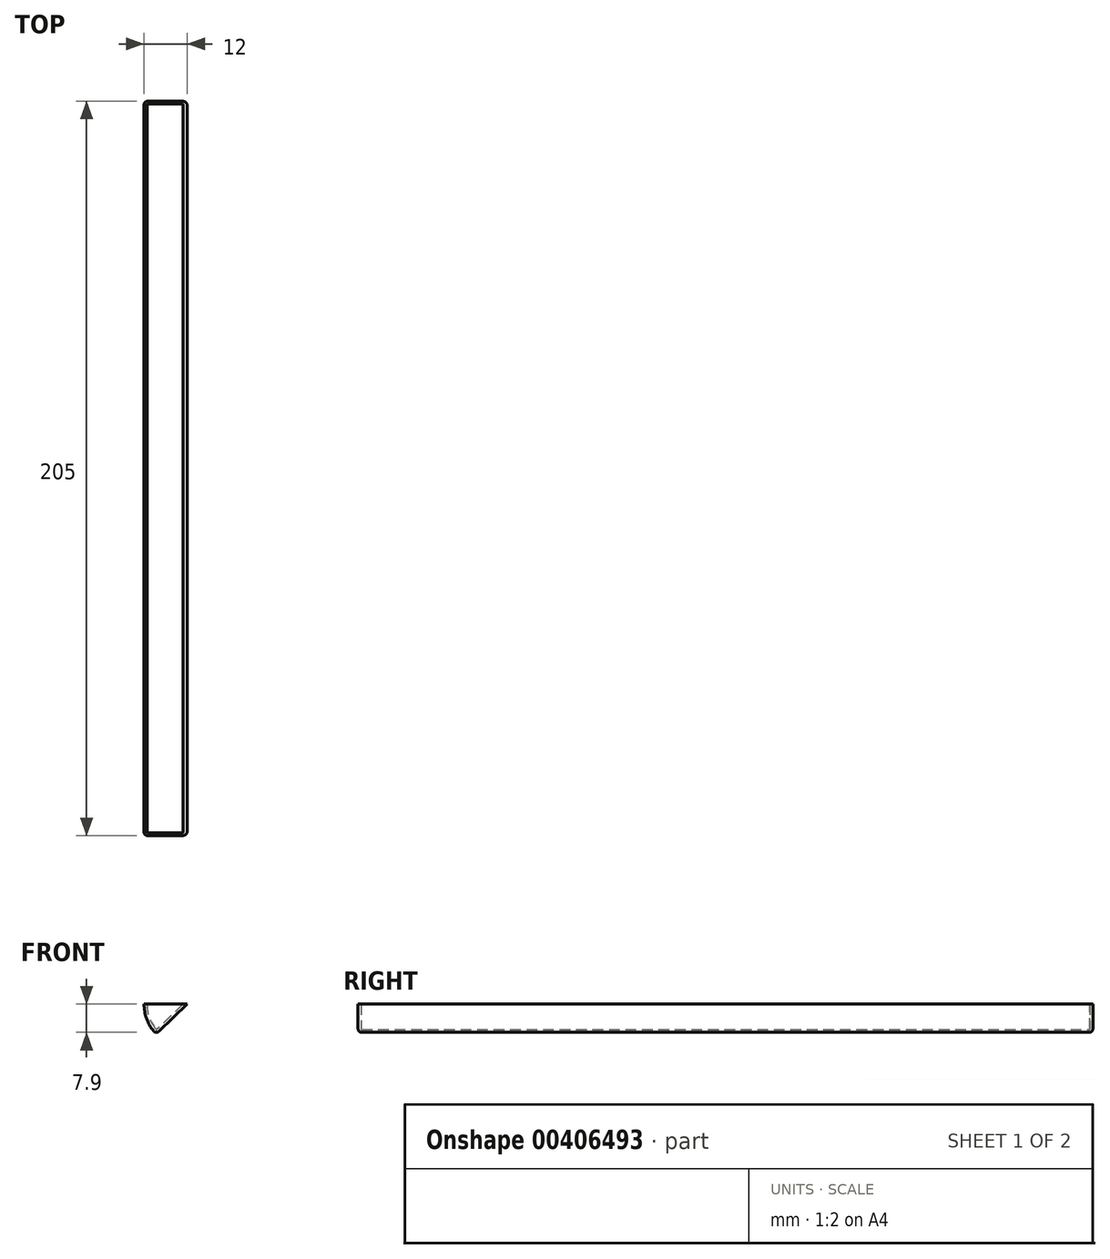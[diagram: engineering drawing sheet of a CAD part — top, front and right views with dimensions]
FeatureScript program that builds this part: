
annotation { "Feature Type Name" : "Feature", "Feature Type Description" : "" }
export const myFeature = defineFeature(function(context is Context, id is Id, definition is map)
    precondition{}
    {
        {
            var Q0;
            Q0=qCreatedBy(makeId("Front.planeOp"),FACE);
            var sketch = newSketch(context, id + "F0", { "sketchPlane" : qUnion([Q0])});
            skPoint(sketch, "E0.middle", {"position": v(0, 0) * mm});
            skLineSegment(sketch, "E1", {"start": v(-12, 0) * mm, "end": v(0, 0) * mm});
            skLineSegment(sketch, "E2", {"start": v(0, 0) * mm, "end": v(-8.62, -8.35) * mm});
            skPoint(sketch, "E0.bottom.start.orphan", {"position": v(-12, 11.63) * mm});
            skPoint(sketch, "E0.right.start.orphan", {"position": v(12, 11.63) * mm});
            skPoint(sketch, "E0.top.end.orphan", {"position": v(12, -11.63) * mm});
            skArc(sketch, "E3", {"start": v(-12, 0) * mm, "mid": v(-11.12, -4.5) * mm, "end": v(-8.62, -8.35) * mm});
            skPoint(sketch, "E4.orphan", {"position": v(-12, -11.63) * mm});
            skSolve(sketch);
        }
        {
            var Q0;
            Q0=makeQuery(id+"F0.imprint","IMPRINT",FACE,{"disambiguationData":[TD([[makeQuery(id+"F0.imprint","IMPRINT",EDGE,{"derivedFrom":sQuery(id+"F0.wireOp",EDGE,"E1")}),-1.0]])]});
            extrude(context, id + "F1", {"entities" : qUnion([Q0]), "depth" : 205 * mm});
        }
        {
            var Q0;
            Q0=makeQuery(id+"F1.opExtrude","SWEPT_EDGE",EDGE,{"disambiguationData":[OSD([sQuery(id+"F0.wireOp",EDGE,"E2"),sQuery(id+"F0.wireOp",EDGE,"E3")])]});
            var Q1;
            Q1=makeQuery(id+"F1.opExtrude","CAP_EDGE",EDGE,{"disambiguationData":[OSD([sQuery(id+"F0.wireOp",EDGE,"E2")])],"isStart":false});
            var Q2;
            Q2=makeQuery(id+"F1.opExtrude","CAP_EDGE",EDGE,{"disambiguationData":[OSD([sQuery(id+"F0.wireOp",EDGE,"E3")])],"isStart":false});
            var Q3;
            Q3=makeQuery(id+"F1.opExtrude","CAP_EDGE",EDGE,{"disambiguationData":[OSD([sQuery(id+"F0.wireOp",EDGE,"E2")])],"isStart":true});
            var Q4;
            Q4=makeQuery(id+"F1.opExtrude","CAP_EDGE",EDGE,{"disambiguationData":[OSD([sQuery(id+"F0.wireOp",EDGE,"E3")])],"isStart":true});
            fillet(context, id + "F2", {"entities" : qUnion([Q0, Q1, Q2, Q3, Q4]), "radius" : 1 * mm, "tangentPropagation" : true, "allowEdgeOverflow" : false});
        }
        {
            var Q0;
            Q0=makeQuery(id+"F1.opExtrude","SWEPT_FACE",FACE,{"disambiguationData":[OSD([sQuery(id+"F0.wireOp",EDGE,"E1")])]});
            shell(context, id + "F3", {"entities" : qUnion([Q0]), "thickness" : .8 * mm});
        }
    });
